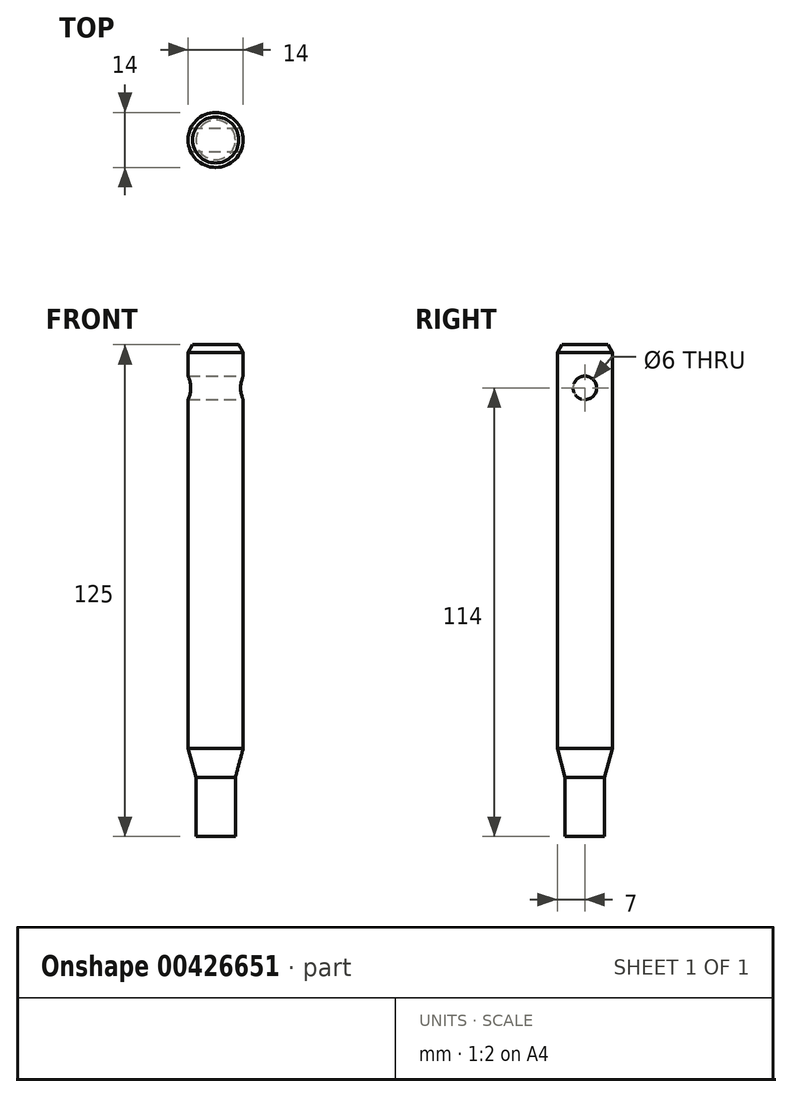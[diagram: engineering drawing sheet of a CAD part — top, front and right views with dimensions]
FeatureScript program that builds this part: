
annotation { "Feature Type Name" : "Feature", "Feature Type Description" : "" }
export const myFeature = defineFeature(function(context is Context, id is Id, definition is map)
    precondition{}
    {
        {
            var Q0;
            Q0=qCreatedBy(makeId("Top.planeOp"),FACE);
            var sketch = newSketch(context, id + "F0", { "sketchPlane" : qUnion([Q0])});
            skCircle(sketch, "E0", {"center": v(0, 0) * mm, "radius": 7 * mm});
            skSolve(sketch);
        }
        {
            var Q0;
            Q0 = qSketchRegion(id + "F0", true);
            extrude(context, id + "F1", {"entities" : qUnion([Q0]), "endBound" : BoundingType.SYMMETRIC, "depth" : 125 * mm, "offsetDistance" : 25 * mm, "hasSecondDirection" : true, "secondDirectionOppositeDirection" : true, "secondDirectionDepth" : 25 * mm});
        }
        {
            var Q0;
            Q0=qCreatedBy(makeId("Right.planeOp"),FACE);
            var sketch = newSketch(context, id + "F2", { "sketchPlane" : qUnion([Q0])});
            skCircle(sketch, "E1", {"center": v(0, 51.5) * mm, "radius": 3 * mm});
            skSolve(sketch);
        }
        {
            var Q0;
            Q0 = qSketchRegion(id + "F2", true);
            extrude(context, id + "F3", {"entities" : qUnion([Q0]), "operationType" : NewBodyOperationType.REMOVE, "endBound" : BoundingType.THROUGH_ALL, "oppositeDirection" : true, "depth" : 25 * mm, "offsetDistance" : 25 * mm, "hasSecondDirection" : true, "secondDirectionBound" : SecondDirectionBoundingType.THROUGH_ALL, "secondDirectionOppositeDirection" : false, "secondDirectionDepth" : 25 * mm});
        }
        {
            var Q0;
            Q0=qCreatedBy(makeId("Right.planeOp"),FACE);
            var sketch = newSketch(context, id + "F4", { "sketchPlane" : qUnion([Q0])});
            skLineSegment(sketch, "E2", {"start": v(-7, -40.04) * mm, "end": v(-5, -47.5) * mm});
            skLineSegment(sketch, "E3", {"start": v(-5, -47.5) * mm, "end": v(-5, -62.5) * mm});
            skLineSegment(sketch, "E4", {"start": v(-5, -62.5) * mm, "end": v(-7, -62.5) * mm});
            skLineSegment(sketch, "E5", {"start": v(-7, -62.5) * mm, "end": v(-7, -40.04) * mm});
            skLineSegment(sketch, "E6", {"start": v(0, -62.5) * mm, "end": v(0, -40.04) * mm, "construction": true});
            skSolve(sketch);
        }
        {
            var Q0;
            Q0 = qSketchRegion(id + "F4", true);
            var Q1;
            Q1=sQuery(id+"F4.wireOp",EDGE,"E6");
            revolve(context, id + "F5", {"operationType" : NewBodyOperationType.REMOVE, "surfaceOperationType" : NewSurfaceOperationType.NEW, "entities" : qUnion([Q0]), "axis" : qUnion([Q1]), "revolveType" : RevolveType.FULL, "oppositeDirection" : true});
        }
        {
            var Q0;
            Q0=makeQuery(id+"F1.opExtrude","CAP_EDGE",EDGE,{"disambiguationData":[OSD([sQuery(id+"F0.wireOp",EDGE,"E0")])],"isStart":false});
            chamfer(context, id + "F6", {"entities" : qUnion([Q0]), "chamferType" : ChamferType.OFFSET_ANGLE, "width" : 2 * mm, "oppositeDirection" : true, "angle" : 30 * degree, "tangentPropagation" : true});
        }
    });
